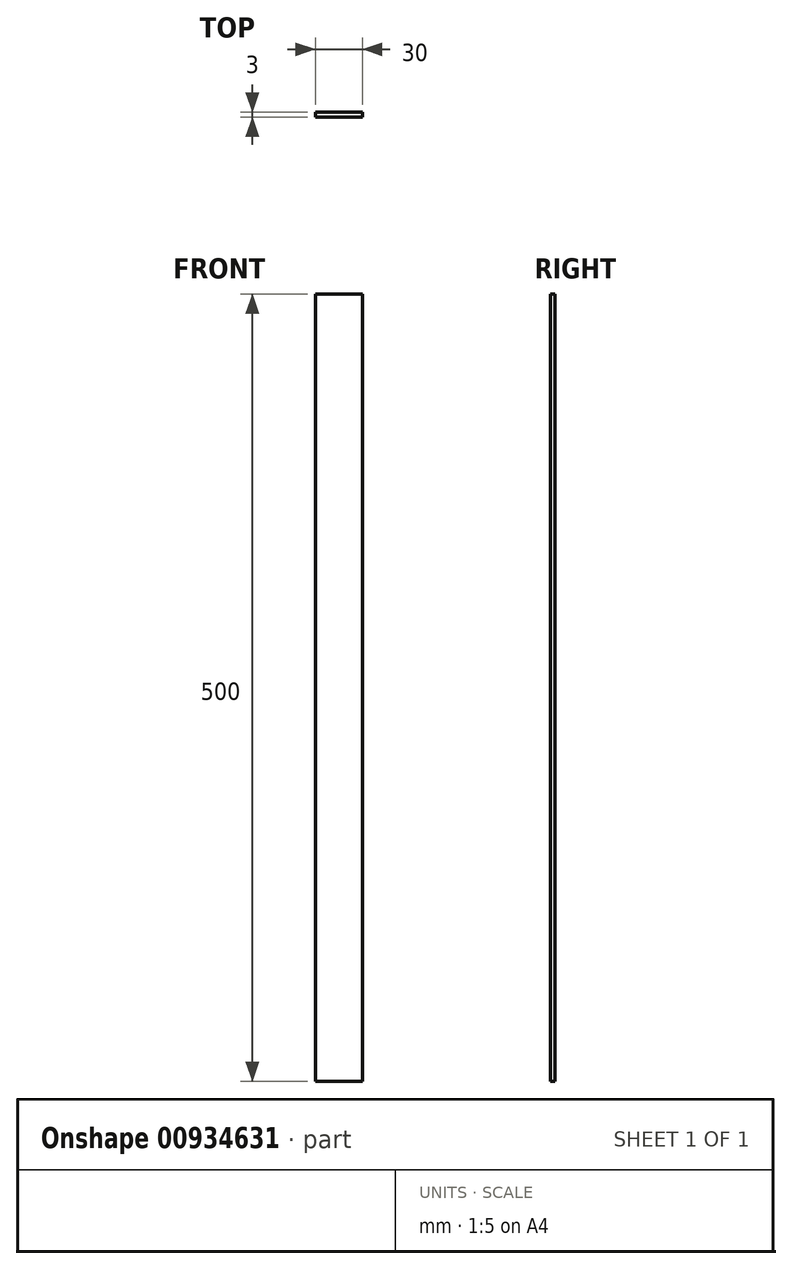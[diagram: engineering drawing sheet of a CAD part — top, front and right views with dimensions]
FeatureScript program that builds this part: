
annotation { "Feature Type Name" : "Feature", "Feature Type Description" : "" }
export const myFeature = defineFeature(function(context is Context, id is Id, definition is map)
    precondition{}
    {
        {
            var Q0;
            Q0=qCreatedBy(makeId("Front.planeOp"),FACE);
            var sketch = newSketch(context, id + "F0", { "sketchPlane" : qUnion([Q0])});
            skLineSegment(sketch, "E0.bottom", {"start": v(0, 0) * mm, "end": v(30, 0) * mm});
            skLineSegment(sketch, "E0.top", {"start": v(0, 500) * mm, "end": v(30, 500) * mm});
            skLineSegment(sketch, "E0.left", {"start": v(0, 0) * mm, "end": v(0, 500) * mm});
            skLineSegment(sketch, "E0.right", {"start": v(30, 0) * mm, "end": v(30, 500) * mm});
            skPoint(sketch, "E1.centerSnap0", {"position": v(15, 500) * mm});
            skSolve(sketch);
        }
        {
            var Q0;
            Q0 = qSketchRegion(id + "F0", true);
            extrude(context, id + "F1", {"entities" : qUnion([Q0]), "depth" : 3 * mm, "offsetDistance" : 25 * mm});
        }
        {
            var Q0;
            Q0=makeQuery(id+"F0.imprint","IMPRINT",FACE,{"disambiguationData":[TD([[makeQuery(id+"F0.imprint","IMPRINT",EDGE,{"derivedFrom":sQuery(id+"F0.wireOp",EDGE,"E0.bottom")}),1.0]])]});
            var sketch = newSketch(context, id + "F2", { "sketchPlane" : qUnion([Q0])});
            skCircle(sketch, "E2", {"center": v(15, 470) * mm, "radius": 4.5 * mm});
            skSolve(sketch);
        }
        {
            var Q0;
            Q0 = qSketchRegion(id + "F2", true);
            extrude(context, id + "F3", {"entities" : qUnion([Q0]), "operationType" : NewBodyOperationType.REMOVE, "endBound" : BoundingType.THROUGH_ALL, "oppositeDirection" : true, "depth" : 25 * mm, "offsetDistance" : 25 * mm});
        }
    });
